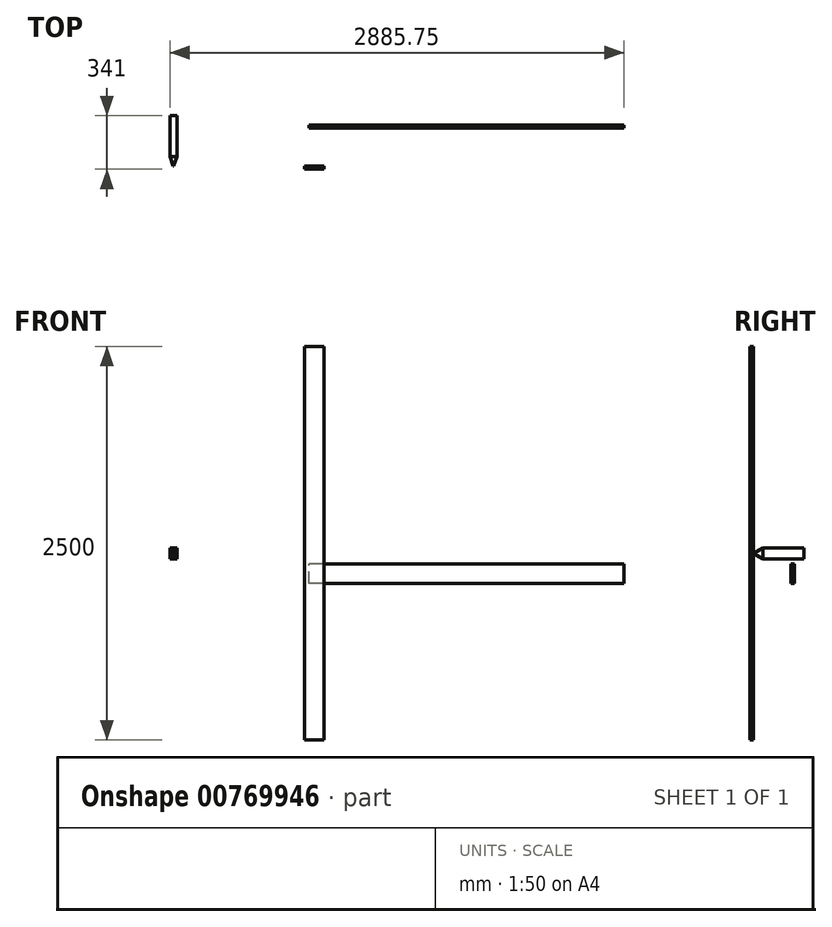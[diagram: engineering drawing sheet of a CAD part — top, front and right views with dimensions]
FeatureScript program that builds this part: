
annotation { "Feature Type Name" : "Feature", "Feature Type Description" : "" }
export const myFeature = defineFeature(function(context is Context, id is Id, definition is map)
    precondition{}
    {
        {
            var Q0;
            Q0=qCreatedBy(makeId("Top.planeOp"),FACE);
            var sketch = newSketch(context, id + "F0", { "sketchPlane" : qUnion([Q0])});
            skLineSegment(sketch, "E0.bottom", {"start": v(-30.45, -3.55) * mm, "end": v(93.55, -3.55) * mm});
            skLineSegment(sketch, "E0.top", {"start": v(-30.45, -24.55) * mm, "end": v(93.55, -24.55) * mm});
            skLineSegment(sketch, "E0.left", {"start": v(-30.45, -3.55) * mm, "end": v(-30.45, -24.55) * mm});
            skLineSegment(sketch, "E0.right", {"start": v(93.55, -3.55) * mm, "end": v(93.55, -24.55) * mm});
            skSolve(sketch);
        }
        {
            var Q0;
            Q0 = qSketchRegion(id + "F0", true);
            extrude(context, id + "F1", {"entities" : qUnion([Q0]), "endBound" : BoundingType.SYMMETRIC, "depth" : 2500 * mm, "offsetDistance" : 25 * mm});
        }
        {
            var Q0;
            Q0=makeQuery(id+"F1.opExtrude","SWEPT_FACE",FACE,{"disambiguationData":[OSD([sQuery(id+"F0.wireOp",EDGE,"E0.bottom")])]});
            var sketch = newSketch(context, id + "F2", { "sketchPlane" : qUnion([Q0])});
            skLineSegment(sketch, "E1.bottom", {"start": v(885.75, -99.86) * mm, "end": v(840.75, -99.86) * mm});
            skLineSegment(sketch, "E1.top", {"start": v(885.75, -29.86) * mm, "end": v(840.75, -29.86) * mm});
            skLineSegment(sketch, "E1.left", {"start": v(885.75, -99.86) * mm, "end": v(885.75, -29.86) * mm});
            skLineSegment(sketch, "E1.right", {"start": v(840.75, -99.86) * mm, "end": v(840.75, -29.86) * mm});
            skSolve(sketch);
        }
        {
            var Q0;
            Q0 = qSketchRegion(id + "F2", true);
            extrude(context, id + "F3", {"entities" : qUnion([Q0]), "depth" : 320 * mm, "offsetDistance" : 25 * mm});
        }
        {
            var Q0;
            Q0=makeQuery(id+"F3.opExtrude","CAP_EDGE",EDGE,{"disambiguationData":[OSD([sQuery(id+"F2.wireOp",EDGE,"E1.right")])],"isStart":true});
            var Q1;
            Q1=makeQuery(id+"F3.opExtrude","CAP_EDGE",EDGE,{"disambiguationData":[OSD([sQuery(id+"F2.wireOp",EDGE,"E1.left")])],"isStart":true});
            chamfer(context, id + "F4", {"entities" : qUnion([Q0, Q1]), "chamferType" : ChamferType.TWO_OFFSETS, "width1" : 22 * mm, "oppositeDirection" : false, "width2" : 60 * mm, "tangentPropagation" : true});
        }
        {
            var Q0;
            Q0=makeQuery(id+"F3.opExtrude","CAP_EDGE",EDGE,{"disambiguationData":[OSD([sQuery(id+"F2.wireOp",EDGE,"E1.bottom")])],"isStart":true});
            var Q1;
            Q1=makeQuery(id+"F3.opExtrude","CAP_EDGE",EDGE,{"disambiguationData":[OSD([sQuery(id+"F2.wireOp",EDGE,"E1.top")])],"isStart":true});
            chamfer(context, id + "F5", {"entities" : qUnion([Q0, Q1]), "chamferType" : ChamferType.TWO_OFFSETS, "width1" : 34.5 * mm, "oppositeDirection" : false, "width2" : 60 * mm, "tangentPropagation" : true});
        }
        {
            var Q0;
            Q0=qCreatedBy(makeId("Right.planeOp"),FACE);
            var sketch = newSketch(context, id + "F6", { "sketchPlane" : qUnion([Q0])});
            skLineSegment(sketch, "E2.bottom", {"start": v(257, -255.17) * mm, "end": v(236, -255.17) * mm});
            skLineSegment(sketch, "E2.top", {"start": v(257, -131.17) * mm, "end": v(236, -131.17) * mm});
            skLineSegment(sketch, "E2.left", {"start": v(257, -255.17) * mm, "end": v(257, -131.17) * mm});
            skLineSegment(sketch, "E2.right", {"start": v(236, -255.17) * mm, "end": v(236, -131.17) * mm});
            skSolve(sketch);
        }
        {
            var Q0;
            Q0 = qSketchRegion(id + "F6", true);
            extrude(context, id + "F7", {"entities" : qUnion([Q0]), "depth" : 2000 * mm, "offsetDistance" : 25 * mm});
        }
    });
